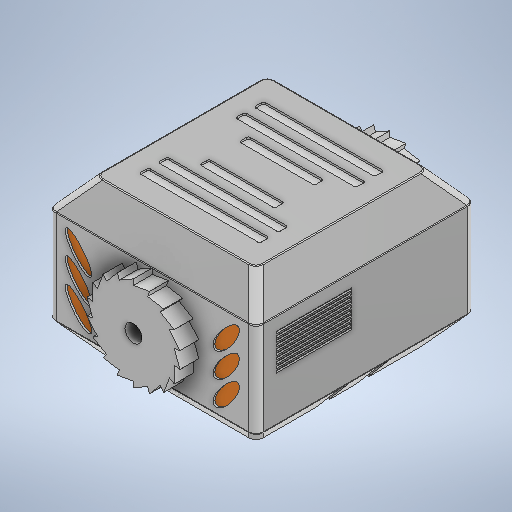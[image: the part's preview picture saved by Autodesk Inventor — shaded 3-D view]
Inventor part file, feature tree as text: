
AUTODESK INVENTOR PART (.ipt)
format: ipt  version: 2025 (Build 290162000, 162)  size: 983,040 bytes
history: native  units: in
note: dims shown in document units (in); Inventor stores cm internally (conversion verified against a paired STEP export)
features: sketch x16, fillet x13, extrude x10, mirror x3, emboss x1
ambient origin geometry x8: Origin, YZ Plane, XZ Plane, XY Plane, X Axis, Y Axis, Z Axis, Center Point
bodies: Solid1 (feature_tree)
feature tree (43):
  extrude  "Extrusion1"  Depth=4.3307in
  extrude  "Extrusion3"  Depth=0.5906in TaperAngle=0.0deg
  extrude  "Extrusion4"  Depth=0.5906in
  sketch  "Sketch11"  dims[d72=0.2362in d73=0.2126in]
  sketch  "Sketch15"  dims[d74=1.5748in d76=0.3937in d77=0.3937in d79=0.3937in d81=0.1811in d82=0.2598in d85=0.2598in d86=0.1811in]
  extrude  "Extrusion12"  Depth=2.9921in
  extrude  "Extrusion13"  Depth=0.3937in
  extrude  "Extrusion14"  Depth=0.3937in
  fillet  "Fillet1"  Radius=0.3937in
  fillet  "Fillet2"  Radius=0.2362in
  fillet  "Fillet3"  Radius=0.1575in
  fillet  "Fillet4"  Radius=0.315in
  extrude  "Extrusion15"  Depth=0.5906in TaperAngle=0.0deg
  extrude  "Extrusion16"  Depth=0.3937in
  fillet  "Fillet5"  Radius=0.0984in
  fillet  "Fillet6"  Radius=0.0984in
  fillet  "Fillet7"  Radius=0.1181in
  fillet  "Fillet8"  Radius=7.0866in
  mirror  "Mirror1"
  fillet  "Fillet9"  Radius=0.3937in
  extrude  "Extrusion17"  Depth=0.2126in
  mirror  "Mirror3"
  mirror  "Mirror4"
  sketch  "Sketch20"  dims[d98=0.0984in]
  extrude  "Extrusion18"  Depth=0.3937in
  fillet  "Fillet10"  Radius=0.2598in
  fillet  "Fillet11"  Radius=0.2598in
  fillet  "Fillet12"  Radius=0.1811in
  fillet  "Fillet14"  Radius=0.0394in
  emboss  "Emboss1"
  sketch  "Sketch1"  dims[d0=4.5669in d1=4.3307in]
  sketch  "Sketch6"  dims[d58=0.1969in d59=0.5906in d60=0.0in]
  sketch  "Sketch7"  dims[d61=0.0984in d62=0.0984in d63=0.0984in d64=0.0984in d65=0.1181in d66=7.0866in d68=360.0deg d70=0.3937in d71=0.0in]
  sketch  "Sketch17"  dims[d87=1.5748in d89=0.3937in d90=0.3937in d92=0.3937in d94=0.0394in d95=0.0in]
  sketch  "Sketch Circular Pattern1"  dims[d2=0.5906in d3=-0.2749in d15=1.9685in d16=0.0in]
  sketch  "Sketch Rectangular Pattern1"  dims[d17=0.5906in d18=-0.2749in d30=1.9685in]
  sketch  "Sketch18"  dims[d96=0.0984in]
  sketch  "Sketch Rectangular Pattern2"  dims[d36=0.3543in d45=2.9921in]
  sketch  "Sketch19"  dims[d97=0.0984in]
  sketch  "Sketch Rectangular Pattern3"  dims[d46=1.1811in d47=0.3937in]
  sketch  "Sketch21"  dims[d99=0.1575in]
  sketch  "Sketch Rectangular Pattern4"  dims[d48=0.3937in d49=2.2047in d50=0.3937in d51=0.2362in d52=0.0in d53=0.1575in d54=0.0in d57=0.315in]
  sketch  "Sketch22"  dims[d100=0.315in d101=0.1969in d102=0.1575in d103=0.2362in d104=1.1811in d106=0.5118in d107=0.3937in d109=0.3937in d111=0.0394in d112=0.0in d113=0.2756in d114=0.2677in d115=1.5748in d116=0.0472in d117=3.937in d119=0.0787in d120=0.3937in d122=0.3937in d124=0.0394in d125=0.0in d126=0.0315in d127=0.0315in d128=0.0315in d130=0.0295in d131=0.1969in d132=0.1969in d133=0.1969in d134=0.1969in d135=0.1969in d136=1.2598in d138=0.0394in d139=0.0394in d141=0.315in d142=0.0394in d143=0.0in d55=0.0197in d56=0.0344in d129=0.0in]
